FCSTD DOCUMENT  (FreeCAD 0.17R13509 (Git))
Label: Trusses
License: All rights reserved
LicenseURL: http://en.wikipedia.org/wiki/All_rights_reserved
objects: Sketcher::SketchObject×1, PartDesign::Body×1
note: 2 computed .brp shape members not serialized (recipe doc carries the construction recipe); baked Part::Feature solids carry a one-line shape summary decoded from their .brp

FEATURE [Sketcher::SketchObject] Sketch
  MapMode = 5
  Support = -> [XY_Plane]
  sketch-geometry (7):
    g0: LineSegment StartX=0 StartY=0 StartZ=0 EndX=8000 EndY=0 EndZ=0
    g1: LineSegment StartX=0 StartY=0 StartZ=0 EndX=4000 EndY=2000 EndZ=0
    g2: LineSegment StartX=8000 StartY=0 StartZ=0 EndX=4000 EndY=2000 EndZ=0
    g3: LineSegment StartX=4000 StartY=2000 StartZ=0 EndX=2845.3 EndY=0 EndZ=0
    g4: LineSegment StartX=2845.3 StartY=0 StartZ=0 EndX=1524.79 EndY=762.396 EndZ=0
    g5: LineSegment StartX=4000 StartY=2000 StartZ=0 EndX=5154.7 EndY=0 EndZ=0
    g6: LineSegment StartX=6475.21 StartY=762.396 StartZ=0 EndX=5154.7 EndY=0 EndZ=0
  constraints (20):
    c: Coincident(g0,g-1)
    c: Horizontal(g0)
    c: Distance(g0) = 8000
    c: Coincident(g1,g-1)
    c: Coincident(g2,g0)
    c: Coincident(g2,g1)
    c: Coincident(g3,g1)
    c: PointOnObject(g3,g0)
    c: Coincident(g4,g3)
    c: PointOnObject(g4,g1)
    c: Angle(g3,g4) = 1.5708
    c: Coincident(g5,g1)
    c: PointOnObject(g5,g0)
    c: PointOnObject(g6,g2)
    c: Coincident(g6,g5)
    c: Angle(g3,g5) = 1.0472
    c: Angle(g6,g5) = 1.5708
    c: DistanceY(g1,g1) = 2000
    c: Equal(g2,g1)
    c: Equal(g3,g5)
FEATURE [PartDesign::Body] Body
  Group = -> [Sketch]
  Origin = -> Origin
